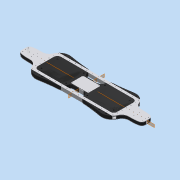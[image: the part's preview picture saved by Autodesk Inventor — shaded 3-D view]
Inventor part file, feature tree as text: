
AUTODESK INVENTOR PART (.ipt)
format: ipt  version: 2015 SP1 (Build 190203100, 203)  size: 3,889,664 bytes
history: native  units: in
note: dims shown in document units (in); Inventor stores cm internally (conversion verified against a paired STEP export)
features: extrude x42, sketch x42, projected_geometry x40, other x34, fillet x31, chamfer x10, plane x9, mirror x8, hole x5, shell x3, split x3
ambient origin geometry x2: Origin, Center Point
bodies: Solid32 (feature_tree)
feature tree (227):
  other  "CrossSection1"
  other  "Curvature1"
  other  "CrossSection2"
  other  "main_support0"
  extrude  "Extrusion1"  Depth=0.75in
  plane  "Work Plane1"
  shell  "Shell2"  Thickness=24.0in
  extrude  "Extrusion33"  Depth=0.125in
  fillet  "Fillet23"  Radius=1.5in
  mirror  "Mirror2"
  extrude  "Extrusion3"  Depth=0.125in TaperAngle=45.0deg
  chamfer  "Chamfer1"  Distance=0.0625in
  fillet  "Fillet3"  Radius=1.0in
  extrude  "Handles"  Depth=0.75in
  fillet  "Fillet4"  Radius=0.0625in
  fillet  "Fillet5"  Radius=0.125in
  plane  "Work Plane2"
  extrude  "Horiz_ Bar"  Depth=5.5in
  shell  "HorizBar_Shell"  Thickness=0.201in
  mirror  "HorizBar_Mirror"
  extrude  "TopPlate_Extrude"  Depth=0.201in
  fillet  "Fillet10"  Radius=0.201in
  chamfer  "Chamfer3"  Distance=0.125in
  fillet  "Fillet6"  Radius=2.0in
  fillet  "Fillet8"  [1 undecoded]
  mirror  "TopPlate_Mirror"
  extrude  "Extrusion9"  Depth=0.75in
  shell  "Shell5"  Thickness=0.0625in
  mirror  "Mirror6"
  extrude  "BottomPlate_TruckMounting"  Depth=0.125in TaperAngle=45.0deg
  fillet  "Fillet9"  Radius=1.0in
  extrude  "Stanoffs"  Depth=0.5in
  mirror  "Mirror9"
  extrude  "Extrusion16"  Depth=0.5in
  extrude  "Extrusion19"  Depth=0.5in TaperAngle=0.0deg
  extrude  "Extrusion20"  TaperAngle=0.0deg  [1 undecoded]
  extrude  "Curvypart"  Depth=0.191in
  extrude  "Extrusion24"  Depth=1.0in TaperAngle=0.0deg
  chamfer  "Chamfer5"  Distance=1.0in
  chamfer  "Chamfer6"  Distance=1.0in
  extrude  "Extrusion93"  Depth=1.0in
  fillet  "Fillet95"  Radius=1.5in
  extrude  "Handlecutout"  Depth=1.375in TaperAngle=45.0deg
  extrude  "Fins"  Depth=1.0in TaperAngle=0.0deg
  extrude  "Heads"  Depth=1.0in
  mirror  "Mirror13"
  fillet  "Fillet20"  Radius=1.0in
  extrude  "Extrusion28"  Depth=0.5in
  plane  "Work Plane6"
  plane  "Work Plane7"
  extrude  "MountSupport_rivetholes"  Depth=1.0in
  fillet  "Fillet28"  Radius=0.191in
  sketch  "Sketch34"  dims[d96=3.0in d106=0.5in]
  extrude  "Extrusion80"  Depth=0.5in
  fillet  "Fillet80"  Radius=5.0in
  fillet  "Fillet81"  Radius=0.75in
  hole  "Hole3"  [1 undecoded]
  hole  "Hole4"  [1 undecoded]
  extrude  "battery cuout"  Depth=0.5in
  fillet  "Fillet58"  Radius=2.0in
  extrude  "Extrusion63"  Depth=2.5in
  extrude  "Extrusion64"  Depth=3.0in
  extrude  "Extrusion65"  Depth=2.0in
  extrude  "bbox_extrude"  Depth=5.9449in
  extrude  "Extrusion67"  Depth=0.0787in
  chamfer  "Chamfer19"  Distance=2.0866in
  fillet  "Fillet59"  Radius=0.25in
  chamfer  "Chamfer20"  Distance=0.25in
  fillet  "Fillet60"  Radius=4.125in
  chamfer  "Chamfer21"  Distance=0.4331in
  fillet  "Fillet61"  Radius=0.0938in
  chamfer  "Chamfer22"  Distance=1.1024in
  fillet  "Fillet62"  Radius=0.5in
  chamfer  "Chamfer23"  Distance=0.375in
  fillet  "Fillet63"  Radius=0.375in
  fillet  "Fillet65"  Radius=1.25in
  fillet  "Fillet69"  Radius=1.0in
  extrude  "Extrusion69"  Depth=1.0in
  chamfer  "Chamfer25"  Distance=0.25in
  fillet  "Fillet83"  Radius=0.9843in
  plane  "Work Plane10"
  hole  "Hole5"  [1 undecoded]
  split  "Split2"
  extrude  "Extrusion76"  Depth=0.125in TaperAngle=45.0deg
  plane  "Work Plane9"
  extrude  "counterbore"  Depth=1.0in
  extrude  "main rivets"  Depth=0.5in TaperAngle=45.0deg
  extrude  "electronics_recess"  Depth=0.5in
  extrude  "Extrusion92"  Depth=0.125in TaperAngle=45.0deg
  fillet  "Fillet93"  Radius=10.0in
  fillet  "Fillet94"  Radius=0.125in
  fillet  "Fillet82"  Radius=10.0in
  extrude  "electronics_plate"  Depth=0.5in TaperAngle=45.0deg
  sketch  "Sketch85"  dims[d219=0.375in d220=0.5in]
  hole  "Hole6"  [1 undecoded]
  hole  "Hole7"  [1 undecoded]
  extrude  "Extrusion87"  Depth=0.5in
  fillet  "Fillet89"  Radius=0.201in
  fillet  "Fillet90"  Radius=0.201in
  extrude  "Extrusion88"  Depth=1.0in
  fillet  "Fillet91"  Radius=0.201in
  fillet  "Fillet92"  Radius=0.75in
  extrude  "Extrusion89"  Depth=1.0in
  sketch  "Sketch96"  dims[d319=0.0787in d348=0.5in]
  split  "Split3"
  split  "Split4"
  extrude  "Extrusion90"  Depth=0.0312in TaperAngle=0.0deg
  extrude  "Extrusion91"  Depth=0.75in
  extrude  "Extrusion94"  Depth=0.75in
  fillet  "Fillet96"  Radius=0.375in
  extrude  "Extrusion95"  Depth=0.5in TaperAngle=0.0deg
  fillet  "Fillet97"  Radius=0.25in
  extrude  "Extrusion96"  Depth=0.25in
  mirror  "Mirror14"
  mirror  "Mirror15"
  plane  "YZ Plane Vertical Spine"
  plane  "XZ Plane Horizontal"
  plane  "XY Plane Vertical Span"
  other  "X Axis Left/Right"
  other  "Y Axis Up/Down"
  other  "Z Axis Fore/Aft"
  sketch  "Sketch1"  dims[d0=0.75in d1=0.75in d2=24.0in d3=0.0in]
  other  "Pattern of main_support0:1"
  other  "main_support1"
  sketch  "Sketch3"  dims[d5=3.25in d6=0.125in d13=1.5in d14=1.5in]
  projected_geometry  "Projected Loop1"
  projected_geometry  "Projected Loop2"
  other  "bottom_plate"
  sketch  "Sketch4"  dims[d16=0.0in d17=1.5in d18=0.125in d19=45.0deg]
  projected_geometry  "Projected Loop3"
  projected_geometry  "Projected Loop4"
  sketch  "Sketch5"  dims[d20=4.0in]
  other  "horiz_support0"
  sketch  "Sketch6"  dims[d22=1.25in]
  other  "top_plate"
  other  "TopPlate_1"
  other  "Pattern of horiz_support0:3"
  other  "horiz_support1"
  sketch  "Sketch9"  dims[d23=6.0in]
  other  "MountSupport_0"
  sketch  "Sketch10"  dims[d24=6.0in d29=0.0625in d30=0.0in d31=1.0in]
  projected_geometry  "Projected Loop10"
  projected_geometry  "Projected Loop11"
  projected_geometry  "Projected Loop12"
  other  "Pattern of top_plate:4"
  other  "MountSupport_1"
  sketch  "Sketch15"  dims[d32=1.0in d33=0.75in d35=0.0625in d36=0.0in d37=0.125in]
  projected_geometry  "Projected Loop20"
  other  "MountStandoffs"
  sketch  "Sketch16"  dims[d41=3.5in d42=5.5in d43=0.201in]
  projected_geometry  "Projected Loop21"
  sketch  "Sketch19"  dims[d44=0.201in d45=0.201in d46=0.201in]
  other  "Printed_Platform"
  sketch  "Sketch23"  dims[d48=1.625in]
  projected_geometry  "Projected Loop28"
  sketch  "Sketch24"  dims[d49=2.5in]
  projected_geometry  "Projected Loop29"
  other  "Printed_Fins"
  sketch  "Sketch26"  dims[d50=0.5in d51=0.125in d52=0.0in d53=2.0in d54=10.0in d62=0.0in d63=0.0in]
  projected_geometry  "Projected Loop36"
  projected_geometry  "Projected Loop37"
  other  "Printed_Heads"
  other  "Printed_Corners"
  sketch  "Sketch27"  dims[d64=0.125in d65=0.75in d66=0.0625in d67=0.0in]
  projected_geometry  "Projected Loop38"
  sketch  "Sketch31"  dims[d73=5.0in d92=0.375in d93=0.125in d94=45.0deg d95=1.0in]
  projected_geometry  "Projected Loop40"
  sketch  "Sketch62"  dims[d107=0.5in d108=0.5in]
  sketch  "Sketch63"  dims[d109=0.5in d110=0.0625in d111=0.0in]
  projected_geometry  "Projected Loop56"
  sketch  "Sketch64"  dims[d113=1.0in d114=0.0in d115=0.0in]
  projected_geometry  "Projected Loop57"
  projected_geometry  "Projected Loop58"
  other  "battery_plate"
  sketch  "Sketch65"  dims[d155=0.191in d156=0.191in]
  projected_geometry  "Projected Loop59"
  projected_geometry  "Projected Loop60"
  other  "battery"
  sketch  "Sketch66"  dims[d157=1.1811in d159=1.25in d160=1.1811in d162=1.25in d165=1.0in d166=0.0in d167=1.0in d168=0.0in]
  projected_geometry  "Projected Loop61"
  projected_geometry  "Projected Loop62"
  other  "batterybox"
  sketch  "Sketch67"  dims[d169=0.0in]
  projected_geometry  "Projected Loop63"
  sketch  "Sketch69"  dims[d170=0.0in]
  projected_geometry  "Projected Loop64"
  sketch  "Sketch72"  dims[d171=18.0in d172=1.0in d173=0.0in]
  projected_geometry  "Projected Loop66"
  projected_geometry  "Projected Loop67"
  sketch  "Sketch78"  dims[d182=1.0in d183=0.0in d184=1.5in d185=1.5in]
  sketch  "Sketch80"  dims[d186=1.0in d187=0.0in d190=0.275in d191=1.375in d192=45.0deg]
  sketch  "Sketch81"  dims[d195=0.275in d196=1.375in d197=45.0deg d198=1.0in d199=0.0in]
  sketch  "Sketch82"  dims[d203=0.0in d204=0.0in d205=1.0in d206=1.0in d207=0.0in]
  projected_geometry  "Projected Loop79"
  sketch  "Sketch83"  dims[d208=0.191in d209=0.5in]
  projected_geometry  "Projected Loop80"
  sketch  "Sketch84"  dims[d210=2.3622in d212=1.125in d213=0.3937in d215=1.0in d217=0.375in d218=0.191in]
  other  "ebox_plate"
  sketch  "Sketch90"  dims[d221=2.3622in d223=1.125in d224=0.3937in d226=1.0in d228=5.0in d229=0.0in d296=0.75in]
  projected_geometry  "Projected Loop86"
  projected_geometry  "Projected Loop87"
  sketch  "Sketch91"  dims[d297=0.75in d298=0.3937in d299=0.0in]
  projected_geometry  "Projected Loop88"
  sketch  "Sketch92"  dims[d300=0.25in d301=0.0in]
  projected_geometry  "Projected Loop92"
  sketch  "Sketch97"  dims[d349=0.201in d350=0.75in d351=0.375in d352=0.25in d353=0.5635in d354=1.0in d355=0.8108in]
  sketch  "Sketch98"  dims[d356=0.159in d357=0.75in d358=0.375in d359=0.313in d360=0.5635in d361=1.0in d362=0.8108in d520=2.0in]
  projected_geometry  "Projected Loop96"
  projected_geometry  "Projected Loop97"
  sketch  "Sketch99"  dims[d522=2.5in d523=2.5in]
  sketch  "Sketch100"  dims[d547=3.0in d548=3.0in]
  projected_geometry  "Projected Loop98"
  projected_geometry  "Projected Loop99"
  sketch  "Sketch101"  dims[d561=0.013in d562=0.5in d563=5.688in d564=2.0in d565=5.9449in]
  projected_geometry  "Projected Loop100"
  projected_geometry  "Projected Loop101"
  projected_geometry  "Projected Loop102"
  sketch  "Sketch102"  dims[d566=2.0866in d567=5.9449in]
  projected_geometry  "Projected Loop103"
  sketch  "Sketch103"  dims[d570=0.3937in d571=0.0in d572=0.0787in d573=2.0866in d574=0.25in d575=0.25in d576=4.125in d577=0.4331in d578=0.0in d579=0.0938in d580=0.0in d581=1.1024in d582=0.0in d583=0.5in d584=0.375in d585=0.375in d586=1.25in d587=1.0in d588=1.0in d589=0.25in d590=0.9843in d591=0.0in d592=0.1875in d593=0.0in d594=0.375in d595=0.125in d596=45.0deg d597=12.0in d598=0.5in d599=0.125in d600=45.0deg d601=0.5in d602=0.125in d603=0.125in d604=45.0deg d605=10.0in d606=0.125in d607=0.125in d608=45.0deg d609=10.0in d610=0.5in d611=0.125in d612=45.0deg d613=1.0in d615=0.125in d626=0.5in d627=0.201in d628=0.201in d629=0.201in d630=0.201in d631=0.75in d632=1.5in d633=0.0312in d634=0.0in d642=0.159in d643=0.75in d644=0.375in d645=0.25in d646=0.5635in d647=1.0in d648=0.8108in d667=0.75in d668=0.75in d669=0.375in d670=0.0in d671=0.013in d672=0.5in d673=0.0in d674=2.0in d691=0.25in d692=0.25in d693=10.0861in d694=0.6562in d695=0.375in d696=0.375in d697=0.375in d698=0.375in d699=1.0in d700=0.0in d701=0.191in d702=0.191in d703=1.0in d704=0.0in d705=3.937in d707=1.625in d708=3.937in d710=1.625in d713=1.0in d714=1.0in d715=0.5938in d716=0.0in d717=8.0in d718=5.0in d719=0.25in d720=0.25in d721=2.5in d722=2.5in d723=0.7in d724=0.0in d725=0.0938in d726=0.0in d727=0.25in d728=0.159in d729=0.75in d730=0.375in d731=0.25in d732=0.5635in d733=1.0in d734=0.8108in d735=0.201in d736=0.75in d737=0.375in d738=0.25in d739=0.5635in d740=1.0in d741=0.8108in d750=0.25in d751=0.125in d752=45.0deg d753=1.0in d767=0.5in d768=0.5in d769=0.125in d770=0.0in d771=0.1875in d772=0.25in d773=0.5in d774=0.25in d775=1.0in d779=0.125in d780=0.0938in d781=0.125in d782=0.0938in d783=0.25in d784=0.25in d785=0.0in d786=0.0in d787=2.0in d788=0.5in d789=1.0in d790=0.0in d791=8.125in d792=-0.2061in d794=2.495in d795=2.495in d798=1.0in d799=0.0in d800=1.0in d801=0.0in d808=0.499in d809=0.25in d810=0.0in d811=0.5in d812=0.125in d813=4.0in d814=0.0in d815=10.0in d816=0.5in d817=0.5in d818=0.5in d819=4.0in d820=0.0in d821=0.25in d822=0.125in d823=0.2405in d824=0.2405in d825=0.75in d826=0.0in d827=0.0312in d829=0.0079in d830=0.75in d831=0.0in d341=1.0in d342=1.0in]
  other  "slidythings"
  other  "batterybox_front"
  other  "bbox_back"
  other  "bbox_front"
  other  "foot0"
  other  "foot1"
  other  "e_center"
note: 7 required parameter values undecoded (feature->parameter linkage not recoverable at this tier; creation-order binding heuristic only, values carry confidence <= 0.55)
